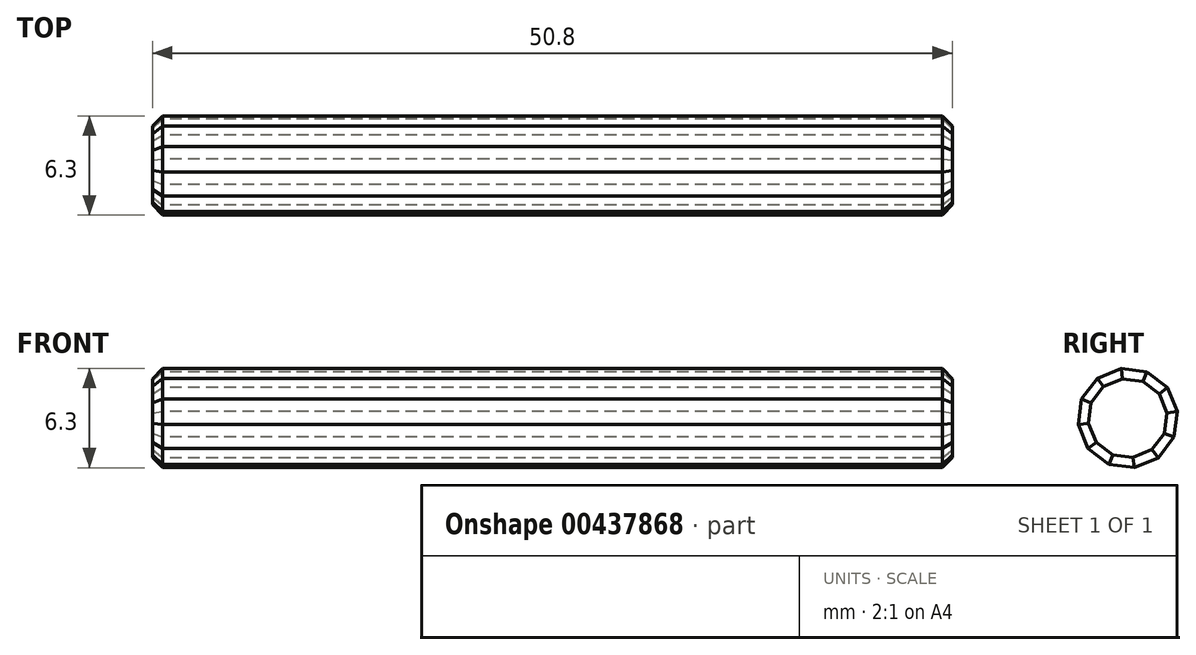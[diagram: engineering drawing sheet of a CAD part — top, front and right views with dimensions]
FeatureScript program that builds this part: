
annotation { "Feature Type Name" : "Feature", "Feature Type Description" : "" }
export const myFeature = defineFeature(function(context is Context, id is Id, definition is map)
    precondition{}
    {
        {
            var Q0;
            Q0=qCreatedBy(makeId("Right.planeOp"),FACE);
            var sketch = newSketch(context, id + "F0", { "sketchPlane" : qUnion([Q0])});
            skCircle(sketch, "E0", {"center": v(0, 0) * mm, "radius": 3.18 * mm, "construction": true});
            skLineSegment(sketch, "E1.0", {"start": v(-1.94, 2.52) * mm, "end": v(-0.42, 3.15) * mm});
            skLineSegment(sketch, "E1.1", {"start": v(-0.42, 3.15) * mm, "end": v(1.21, 2.93) * mm});
            skLineSegment(sketch, "E1.2", {"start": v(1.21, 2.93) * mm, "end": v(2.52, 1.94) * mm});
            skLineSegment(sketch, "E1.3", {"start": v(2.52, 1.94) * mm, "end": v(3.15, 0.42) * mm});
            skLineSegment(sketch, "E1.4", {"start": v(3.15, 0.42) * mm, "end": v(2.93, -1.21) * mm});
            skLineSegment(sketch, "E1.5", {"start": v(2.93, -1.21) * mm, "end": v(1.94, -2.52) * mm});
            skLineSegment(sketch, "E1.6", {"start": v(1.94, -2.52) * mm, "end": v(0.42, -3.15) * mm});
            skLineSegment(sketch, "E1.7", {"start": v(0.42, -3.15) * mm, "end": v(-1.21, -2.93) * mm});
            skLineSegment(sketch, "E1.8", {"start": v(-1.21, -2.93) * mm, "end": v(-2.52, -1.94) * mm});
            skLineSegment(sketch, "E1.9", {"start": v(-2.52, -1.94) * mm, "end": v(-3.15, -0.42) * mm});
            skLineSegment(sketch, "E1.10", {"start": v(-3.15, -0.42) * mm, "end": v(-2.93, 1.21) * mm});
            skLineSegment(sketch, "E1.11", {"start": v(-2.93, 1.21) * mm, "end": v(-1.94, 2.52) * mm});
            skSolve(sketch);
        }
        {
            var Q0;
            Q0=makeQuery(id+"F0.imprint","IMPRINT",FACE,{"disambiguationData":[TD([[makeQuery(id+"F0.imprint","IMPRINT",EDGE,{"derivedFrom":sQuery(id+"F0.wireOp",EDGE,"E1.0")}),-1.0]])]});
            extrude(context, id + "F1", {"entities" : qUnion([Q0]), "depth" : 50.8 * mm, "symmetric" : true});
        }
        {
            var Q0;
            Q0=makeQuery(id+"F1.opExtrude","CAP_FACE",FACE,{"disambiguationData":[OSD([sQuery(id+"F0.wireOp",EDGE,"E1.0"),sQuery(id+"F0.wireOp",EDGE,"E1.1"),sQuery(id+"F0.wireOp",EDGE,"E1.2"),sQuery(id+"F0.wireOp",EDGE,"E1.3"),sQuery(id+"F0.wireOp",EDGE,"E1.4"),sQuery(id+"F0.wireOp",EDGE,"E1.5"),sQuery(id+"F0.wireOp",EDGE,"E1.6"),sQuery(id+"F0.wireOp",EDGE,"E1.7"),sQuery(id+"F0.wireOp",EDGE,"E1.8"),sQuery(id+"F0.wireOp",EDGE,"E1.9"),sQuery(id+"F0.wireOp",EDGE,"E1.10"),sQuery(id+"F0.wireOp",EDGE,"E1.11")])],"isStart":false});
            var Q1;
            Q1=makeQuery(id+"F1.opExtrude","CAP_FACE",FACE,{"disambiguationData":[OSD([sQuery(id+"F0.wireOp",EDGE,"E1.0"),sQuery(id+"F0.wireOp",EDGE,"E1.1"),sQuery(id+"F0.wireOp",EDGE,"E1.2"),sQuery(id+"F0.wireOp",EDGE,"E1.3"),sQuery(id+"F0.wireOp",EDGE,"E1.4"),sQuery(id+"F0.wireOp",EDGE,"E1.5"),sQuery(id+"F0.wireOp",EDGE,"E1.6"),sQuery(id+"F0.wireOp",EDGE,"E1.7"),sQuery(id+"F0.wireOp",EDGE,"E1.8"),sQuery(id+"F0.wireOp",EDGE,"E1.9"),sQuery(id+"F0.wireOp",EDGE,"E1.10"),sQuery(id+"F0.wireOp",EDGE,"E1.11")])],"isStart":true});
            chamfer(context, id + "F2", {"entities" : qUnion([Q0, Q1]), "width" : 0.64 * mm, "tangentPropagation" : true});
        }
    });
